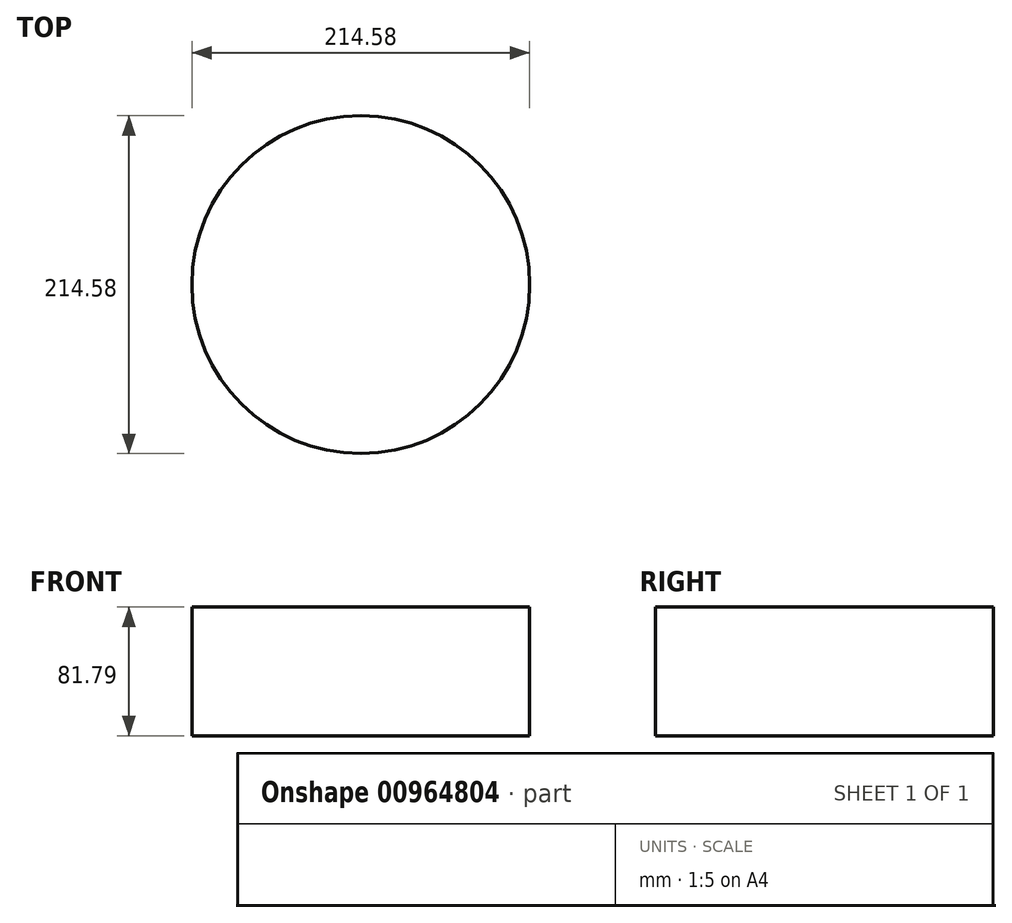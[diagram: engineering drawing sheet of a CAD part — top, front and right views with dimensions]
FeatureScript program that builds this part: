
annotation { "Feature Type Name" : "Feature", "Feature Type Description" : "" }
export const myFeature = defineFeature(function(context is Context, id is Id, definition is map)
    precondition{}
    {
        {
            var Q0;
            Q0=qCreatedBy(makeId("Top.planeOp"),FACE);
            var sketch = newSketch(context, id + "F0", { "sketchPlane" : qUnion([Q0])});
            skCircle(sketch, "E0", {"center": v(0, 0) * mm, "radius": 107.3 * mm});
            skSolve(sketch);
        }
        {
            var Q0;
            Q0=makeQuery(id+"F0.imprint","IMPRINT",FACE,{"disambiguationData":[TD([[makeQuery(id+"F0.imprint","IMPRINT",EDGE,{"derivedFrom":sQuery(id+"F0.wireOp",EDGE,"E0")}),1.0]])]});
            extrude(context, id + "F1", {"entities" : qUnion([Q0]), "depth" : 81.8 * mm, "offsetDistance" : 25.4 * mm});
        }
    });
